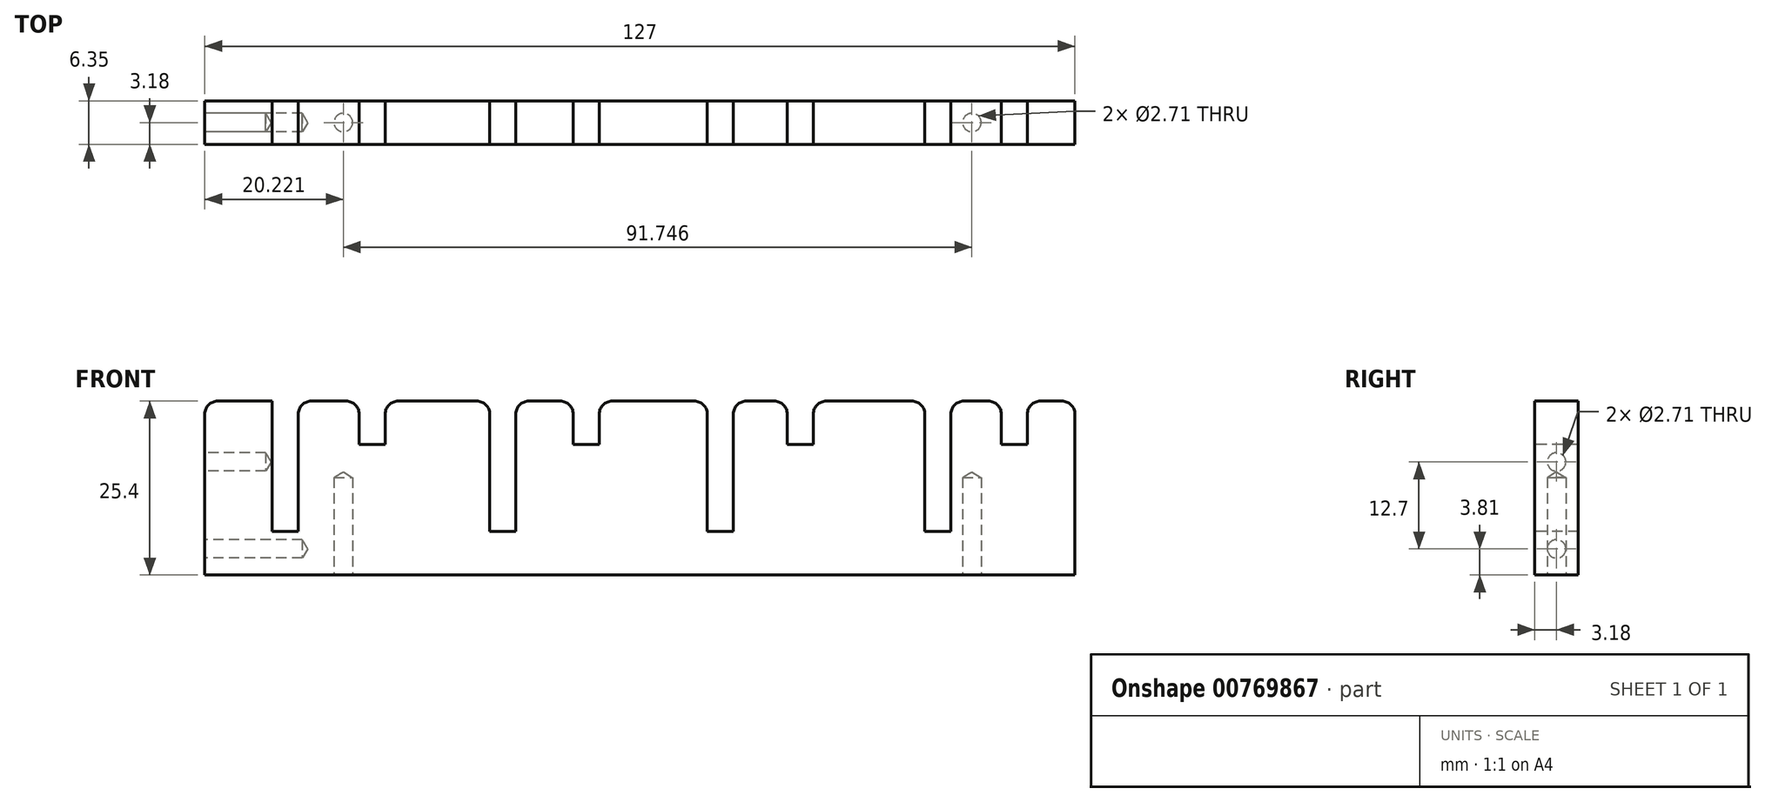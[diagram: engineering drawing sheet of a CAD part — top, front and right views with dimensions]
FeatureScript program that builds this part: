
annotation { "Feature Type Name" : "Feature", "Feature Type Description" : "" }
export const myFeature = defineFeature(function(context is Context, id is Id, definition is map)
    precondition{}
    {
        {
            var Q0;
            Q0=qCreatedBy(makeId("Top.planeOp"),FACE);
            var sketch = newSketch(context, id + "F0", { "sketchPlane" : qUnion([Q0])});
            skLineSegment(sketch, "E0.bottom", {"start": v(-63.5, 3.18) * mm, "end": v(63.5, 3.18) * mm});
            skLineSegment(sketch, "E0.top", {"start": v(-63.5, -3.17) * mm, "end": v(63.5, -3.17) * mm});
            skLineSegment(sketch, "E0.left", {"start": v(-63.5, 3.18) * mm, "end": v(-63.5, -3.17) * mm});
            skLineSegment(sketch, "E0.right", {"start": v(63.5, 3.18) * mm, "end": v(63.5, -3.17) * mm});
            skLineSegment(sketch, "E1", {"start": v(-63.5, 3.18) * mm, "end": v(63.5, -3.17) * mm, "construction": true});
            skPoint(sketch, "E2", {"position": v(0, 0) * mm});
            skSolve(sketch);
        }
        {
            var Q0;
            Q0=qSketchRegion(id+"F0",true);
            extrude(context, id + "F1", {"entities" : qUnion([Q0]), "depth" : 25.4 * mm, "offsetDistance" : 25.4 * mm});
        }
        {
            var Q0;
            Q0=makeQuery(id+"F1.opExtrude","SWEPT_FACE",FACE,{"disambiguationData":[OSD([sQuery(id+"F0.wireOp",EDGE,"E0.top")])]});
            var sketch = newSketch(context, id + "F2", { "sketchPlane" : qUnion([Q0])});
            skLineSegment(sketch, "E3", {"start": v(-53.66, 25.4) * mm, "end": v(-53.66, 6.35) * mm});
            skLineSegment(sketch, "E4", {"start": v(-53.66, 6.35) * mm, "end": v(-49.85, 6.35) * mm});
            skLineSegment(sketch, "E5", {"start": v(-49.85, 6.35) * mm, "end": v(-49.85, 25.4) * mm});
            skLineSegment(sketch, "E6", {"start": v(-53.66, 25.4) * mm, "end": v(-49.85, 25.4) * mm});
            skLineSegment(sketch, "E7.1.0.0", {"start": v(-21.9, 25.4) * mm, "end": v(-18.1, 25.4) * mm});
            skLineSegment(sketch, "E7.1.0.1", {"start": v(-21.9, 25.4) * mm, "end": v(-21.9, 6.35) * mm});
            skLineSegment(sketch, "E7.1.0.2", {"start": v(-18.1, 6.35) * mm, "end": v(-18.1, 25.4) * mm});
            skLineSegment(sketch, "E7.1.0.3", {"start": v(-21.9, 6.35) * mm, "end": v(-18.1, 6.35) * mm});
            skLineSegment(sketch, "E7.2.0.0", {"start": v(9.84, 25.4) * mm, "end": v(13.65, 25.4) * mm});
            skLineSegment(sketch, "E7.2.0.1", {"start": v(9.84, 25.4) * mm, "end": v(9.84, 6.35) * mm});
            skLineSegment(sketch, "E7.2.0.2", {"start": v(13.65, 6.35) * mm, "end": v(13.65, 25.4) * mm});
            skLineSegment(sketch, "E7.2.0.3", {"start": v(9.84, 6.35) * mm, "end": v(13.65, 6.35) * mm});
            skLineSegment(sketch, "E7.3.0.0", {"start": v(41.6, 25.4) * mm, "end": v(45.4, 25.4) * mm});
            skLineSegment(sketch, "E7.3.0.1", {"start": v(41.6, 25.4) * mm, "end": v(41.6, 6.35) * mm});
            skLineSegment(sketch, "E7.3.0.2", {"start": v(45.4, 6.35) * mm, "end": v(45.4, 25.4) * mm});
            skLineSegment(sketch, "E7.3.0.3", {"start": v(41.6, 6.35) * mm, "end": v(45.4, 6.35) * mm});
            skLineSegment(sketch, "E7.direction1", {"start": v(-53.66, 6.35) * mm, "end": v(-21.9, 6.35) * mm, "construction": true});
            skPoint(sketch, "E8", {"position": v(-51.75, 6.35) * mm});
            skLineSegment(sketch, "E9.bottom", {"start": v(-40.97, 25.4) * mm, "end": v(-37.16, 25.4) * mm});
            skLineSegment(sketch, "E9.top", {"start": v(-40.97, 19.05) * mm, "end": v(-37.16, 19.05) * mm});
            skLineSegment(sketch, "E9.left", {"start": v(-40.97, 25.4) * mm, "end": v(-40.97, 19.05) * mm});
            skLineSegment(sketch, "E9.right", {"start": v(-37.16, 25.4) * mm, "end": v(-37.16, 19.05) * mm});
            skLineSegment(sketch, "E10.1.0.0", {"start": v(-5.92, 25.4) * mm, "end": v(-5.92, 19.05) * mm});
            skLineSegment(sketch, "E10.1.0.1", {"start": v(-9.73, 19.05) * mm, "end": v(-5.92, 19.05) * mm});
            skLineSegment(sketch, "E10.1.0.2", {"start": v(-9.73, 25.4) * mm, "end": v(-5.92, 25.4) * mm});
            skLineSegment(sketch, "E10.1.0.3", {"start": v(-9.73, 25.4) * mm, "end": v(-9.73, 19.05) * mm});
            skLineSegment(sketch, "E10.2.0.0", {"start": v(25.32, 25.4) * mm, "end": v(25.32, 19.05) * mm});
            skLineSegment(sketch, "E10.2.0.1", {"start": v(21.51, 19.05) * mm, "end": v(25.32, 19.05) * mm});
            skLineSegment(sketch, "E10.2.0.2", {"start": v(21.51, 25.4) * mm, "end": v(25.32, 25.4) * mm});
            skLineSegment(sketch, "E10.2.0.3", {"start": v(21.51, 25.4) * mm, "end": v(21.51, 19.05) * mm});
            skLineSegment(sketch, "E10.3.0.0", {"start": v(56.57, 25.4) * mm, "end": v(56.57, 19.05) * mm});
            skLineSegment(sketch, "E10.3.0.1", {"start": v(52.76, 19.05) * mm, "end": v(56.57, 19.05) * mm});
            skLineSegment(sketch, "E10.3.0.2", {"start": v(52.76, 25.4) * mm, "end": v(56.57, 25.4) * mm});
            skLineSegment(sketch, "E10.3.0.3", {"start": v(52.76, 25.4) * mm, "end": v(52.76, 19.05) * mm});
            skLineSegment(sketch, "E10.direction1", {"start": v(-40.97, 19.05) * mm, "end": v(-9.73, 19.05) * mm, "construction": true});
            skPoint(sketch, "E11", {"position": v(-39.07, 25.4) * mm});
            skLineSegment(sketch, "E12", {"start": v(-49.85, 15.88) * mm, "end": v(-21.9, 15.88) * mm, "construction": true});
            skLineSegment(sketch, "E13", {"start": v(-35.88, 15.88) * mm, "end": v(-35.88, 0) * mm, "construction": true});
            skSolve(sketch);
        }
        {
            var Q0;
            Q0=qSketchRegion(id+"F2",true);
            extrude(context, id + "F3", {"entities" : qUnion([Q0]), "operationType" : NewBodyOperationType.REMOVE, "endBound" : BoundingType.UP_TO_NEXT, "oppositeDirection" : true, "depth" : 25.4 * mm, "offsetDistance" : 25.4 * mm});
        }
        {
            var Q0;
            Q0=makeQuery(id+"F3.boolean.opBoolean","COPY",EDGE,{"derivedFrom":makeQuery(id+"F3.opExtrude","SWEPT_EDGE",EDGE,{"disambiguationData":[OSD([sQuery(id+"F0.wireOp",EDGE,"E0.top"),sQuery(id+"F2.wireOp",EDGE,"E3"),sQuery(id+"F2.wireOp",EDGE,"E6")])]})});
            var Q1;
            Q1=makeQuery(id+"F3.boolean.opBoolean","COPY",EDGE,{"derivedFrom":makeQuery(id+"F3.opExtrude","SWEPT_EDGE",EDGE,{"disambiguationData":[OSD([sQuery(id+"F0.wireOp",EDGE,"E0.top"),sQuery(id+"F2.wireOp",EDGE,"E5"),sQuery(id+"F2.wireOp",EDGE,"E6")])]})});
            var Q2;
            Q2=makeQuery(id+"F3.boolean.opBoolean","COPY",EDGE,{"derivedFrom":makeQuery(id+"F3.opExtrude","SWEPT_EDGE",EDGE,{"disambiguationData":[OSD([sQuery(id+"F0.wireOp",EDGE,"E0.top"),sQuery(id+"F2.wireOp",EDGE,"E7.1.0.0"),sQuery(id+"F2.wireOp",EDGE,"E7.1.0.1")])]})});
            var Q3;
            Q3=makeQuery(id+"F3.boolean.opBoolean","COPY",EDGE,{"derivedFrom":makeQuery(id+"F3.opExtrude","SWEPT_EDGE",EDGE,{"disambiguationData":[OSD([sQuery(id+"F0.wireOp",EDGE,"E0.top"),sQuery(id+"F2.wireOp",EDGE,"E7.1.0.0"),sQuery(id+"F2.wireOp",EDGE,"E7.1.0.2")])]})});
            var Q4;
            Q4=makeQuery(id+"F3.boolean.opBoolean","COPY",EDGE,{"derivedFrom":makeQuery(id+"F3.opExtrude","SWEPT_EDGE",EDGE,{"disambiguationData":[OSD([sQuery(id+"F0.wireOp",EDGE,"E0.top"),sQuery(id+"F2.wireOp",EDGE,"E7.2.0.0"),sQuery(id+"F2.wireOp",EDGE,"E7.2.0.1")])]})});
            var Q5;
            Q5=makeQuery(id+"F3.boolean.opBoolean","COPY",EDGE,{"derivedFrom":makeQuery(id+"F3.opExtrude","SWEPT_EDGE",EDGE,{"disambiguationData":[OSD([sQuery(id+"F0.wireOp",EDGE,"E0.top"),sQuery(id+"F2.wireOp",EDGE,"E7.2.0.0"),sQuery(id+"F2.wireOp",EDGE,"E7.2.0.2")])]})});
            var Q6;
            Q6=makeQuery(id+"F3.boolean.opBoolean","COPY",EDGE,{"derivedFrom":makeQuery(id+"F3.opExtrude","SWEPT_EDGE",EDGE,{"disambiguationData":[OSD([sQuery(id+"F0.wireOp",EDGE,"E0.top"),sQuery(id+"F2.wireOp",EDGE,"E7.3.0.0"),sQuery(id+"F2.wireOp",EDGE,"E7.3.0.1")])]})});
            var Q7;
            Q7=makeQuery(id+"F3.boolean.opBoolean","COPY",EDGE,{"derivedFrom":makeQuery(id+"F3.opExtrude","SWEPT_EDGE",EDGE,{"disambiguationData":[OSD([sQuery(id+"F0.wireOp",EDGE,"E0.top"),sQuery(id+"F2.wireOp",EDGE,"E7.3.0.0"),sQuery(id+"F2.wireOp",EDGE,"E7.3.0.2")])]})});
            var Q8;
            Q8=makeQuery(id+"F3.boolean.opBoolean","COPY",EDGE,{"derivedFrom":makeQuery(id+"F3.opExtrude","SWEPT_EDGE",EDGE,{"disambiguationData":[OSD([sQuery(id+"F0.wireOp",EDGE,"E0.top"),sQuery(id+"F2.wireOp",EDGE,"E9.bottom"),sQuery(id+"F2.wireOp",EDGE,"E9.left")])]})});
            var Q9;
            Q9=makeQuery(id+"F3.boolean.opBoolean","COPY",EDGE,{"derivedFrom":makeQuery(id+"F3.opExtrude","SWEPT_EDGE",EDGE,{"disambiguationData":[OSD([sQuery(id+"F0.wireOp",EDGE,"E0.top"),sQuery(id+"F2.wireOp",EDGE,"E9.bottom"),sQuery(id+"F2.wireOp",EDGE,"E9.right")])]})});
            var Q10;
            Q10=makeQuery(id+"F3.boolean.opBoolean","COPY",EDGE,{"derivedFrom":makeQuery(id+"F3.opExtrude","SWEPT_EDGE",EDGE,{"disambiguationData":[OSD([sQuery(id+"F0.wireOp",EDGE,"E0.top"),sQuery(id+"F2.wireOp",EDGE,"E10.1.0.2"),sQuery(id+"F2.wireOp",EDGE,"E10.1.0.3")])]})});
            var Q11;
            Q11=makeQuery(id+"F3.boolean.opBoolean","COPY",EDGE,{"derivedFrom":makeQuery(id+"F3.opExtrude","SWEPT_EDGE",EDGE,{"disambiguationData":[OSD([sQuery(id+"F0.wireOp",EDGE,"E0.top"),sQuery(id+"F2.wireOp",EDGE,"E10.1.0.0"),sQuery(id+"F2.wireOp",EDGE,"E10.1.0.2")])]})});
            var Q12;
            Q12=makeQuery(id+"F3.boolean.opBoolean","COPY",EDGE,{"derivedFrom":makeQuery(id+"F3.opExtrude","SWEPT_EDGE",EDGE,{"disambiguationData":[OSD([sQuery(id+"F0.wireOp",EDGE,"E0.top"),sQuery(id+"F2.wireOp",EDGE,"E10.2.0.2"),sQuery(id+"F2.wireOp",EDGE,"E10.2.0.3")])]})});
            var Q13;
            Q13=makeQuery(id+"F3.boolean.opBoolean","COPY",EDGE,{"derivedFrom":makeQuery(id+"F3.opExtrude","SWEPT_EDGE",EDGE,{"disambiguationData":[OSD([sQuery(id+"F0.wireOp",EDGE,"E0.top"),sQuery(id+"F2.wireOp",EDGE,"E10.2.0.0"),sQuery(id+"F2.wireOp",EDGE,"E10.2.0.2")])]})});
            var Q14;
            Q14=makeQuery(id+"F3.boolean.opBoolean","COPY",EDGE,{"derivedFrom":makeQuery(id+"F3.opExtrude","SWEPT_EDGE",EDGE,{"disambiguationData":[OSD([sQuery(id+"F0.wireOp",EDGE,"E0.top"),sQuery(id+"F2.wireOp",EDGE,"E10.3.0.2"),sQuery(id+"F2.wireOp",EDGE,"E10.3.0.3")])]})});
            var Q15;
            Q15=makeQuery(id+"F3.boolean.opBoolean","COPY",EDGE,{"derivedFrom":makeQuery(id+"F3.opExtrude","SWEPT_EDGE",EDGE,{"disambiguationData":[OSD([sQuery(id+"F0.wireOp",EDGE,"E0.top"),sQuery(id+"F2.wireOp",EDGE,"E10.3.0.0"),sQuery(id+"F2.wireOp",EDGE,"E10.3.0.2")])]})});
            var Q16;
            Q16=makeQuery(id+"F1.opExtrude","CAP_EDGE",EDGE,{"disambiguationData":[OSD([sQuery(id+"F0.wireOp",EDGE,"E0.right")])],"isStart":false});
            var Q17;
            Q17=makeQuery(id+"F1.opExtrude","CAP_EDGE",EDGE,{"disambiguationData":[OSD([sQuery(id+"F0.wireOp",EDGE,"E0.left")])],"isStart":false});
            fillet(context, id + "F4", {"entities" : qUnion([Q0, Q1, Q2, Q3, Q4, Q5, Q6, Q7, Q8, Q9, Q10, Q11, Q12, Q13, Q14, Q15, Q16, Q17]), "radius" : 1.9 * mm, "tangentPropagation" : true, "allowEdgeOverflow" : false});
        }
        {
            var Q0;
            Q0=makeQuery(id+"F1.opExtrude","CAP_FACE",FACE,{"disambiguationData":[OSD([sQuery(id+"F0.wireOp",EDGE,"E0.bottom"),sQuery(id+"F0.wireOp",EDGE,"E0.top"),sQuery(id+"F0.wireOp",EDGE,"E0.left"),sQuery(id+"F0.wireOp",EDGE,"E0.right")])],"isStart":true});
            var sketch = newSketch(context, id + "F5", { "sketchPlane" : qUnion([Q0])});
            skLineSegment(sketch, "E14", {"start": v(-63.5, 0) * mm, "end": v(63.5, 0) * mm, "construction": true});
            skPoint(sketch, "E15", {"position": v(-43.28, 0) * mm});
            skPoint(sketch, "E16", {"position": v(48.47, 0) * mm});
            skSolve(sketch);
        }
        {
            var Q0;
            Q0=makeQuery(id+"F1.opExtrude","SWEPT_FACE",FACE,{"disambiguationData":[OSD([sQuery(id+"F0.wireOp",EDGE,"E0.left")])]});
            var sketch = newSketch(context, id + "F6", { "sketchPlane" : qUnion([Q0])});
            skLineSegment(sketch, "E17", {"start": v(0, 23.5) * mm, "end": v(0, 0) * mm, "construction": true});
            skPoint(sketch, "E18", {"position": v(0, 3.81) * mm});
            skPoint(sketch, "E19", {"position": v(0, 16.51) * mm});
            skSolve(sketch);
        }
        {
            var Q0;
            Q0=sQuery(id+"F5.wireOp",VERTEX,"E15");
            var Q1;
            Q1=sQuery(id+"F5.wireOp",VERTEX,"E16");
            var Q2;
            Q2=sQuery(id+"F6.wireOp",VERTEX,"E18");
            var Q3;
            Q3=makeQuery(id+"F1.opExtrude","SWEPT_BODY",BODY,{"disambiguationData":[OSD([sQuery(id+"F0.wireOp",EDGE,"E0.bottom"),sQuery(id+"F0.wireOp",EDGE,"E0.top"),sQuery(id+"F0.wireOp",EDGE,"E0.left"),sQuery(id+"F0.wireOp",EDGE,"E0.right")])]});
            hole(context, id + "F7", {"style" : HoleStyle.SIMPLE, "endStyle" : HoleEndStyle.BLIND, "standardTappedOrClearance" : lookupTablePath({ "standard" : "ANSI", "engagement" : "75%", "pitch" : "32 tpi", "size" : "#6", "type" : "Tapped" }), "standardBlindInLast" : lookupTablePath({ "standard" : "ANSI", "engagement" : "75%", "pitch" : "32 tpi", "size" : "#6", "type" : "Tapped" }), "holeDiameter" : 2.7 * mm, "majorDiameter" : 3.5 * mm, "showTappedDepth" : true, "holeDepth" : 14.22 * mm, "tappedDepth" : 11.84 * mm, "tapClearance" : 3, "locations" : qUnion([Q0, Q1, Q2]), "scope" : qUnion([Q3])});
        }
        {
            var Q0;
            Q0=sQuery(id+"F6.wireOp",VERTEX,"E19");
            var Q1;
            Q1=makeQuery(id+"F1.opExtrude","SWEPT_BODY",BODY,{"disambiguationData":[OSD([sQuery(id+"F0.wireOp",EDGE,"E0.bottom"),sQuery(id+"F0.wireOp",EDGE,"E0.top"),sQuery(id+"F0.wireOp",EDGE,"E0.left"),sQuery(id+"F0.wireOp",EDGE,"E0.right")])]});
            hole(context, id + "F8", {"style" : HoleStyle.SIMPLE, "endStyle" : HoleEndStyle.BLIND, "standardTappedOrClearance" : lookupTablePath({ "standard" : "ANSI", "engagement" : "75%", "pitch" : "32 tpi", "size" : "#6", "type" : "Tapped" }), "standardBlindInLast" : lookupTablePath({ "fit" : "Free", "standard" : "ANSI", "engagement" : "75%", "pitch" : "32 tpi", "size" : "#6", "type" : "Clearance & tapped" }), "holeDiameter" : 2.7 * mm, "majorDiameter" : 3.5 * mm, "showTappedDepth" : true, "holeDepth" : 8.9 * mm, "tappedDepth" : 6.5 * mm, "tapClearance" : 3, "locations" : qUnion([Q0]), "scope" : qUnion([Q1])});
        }
    });
